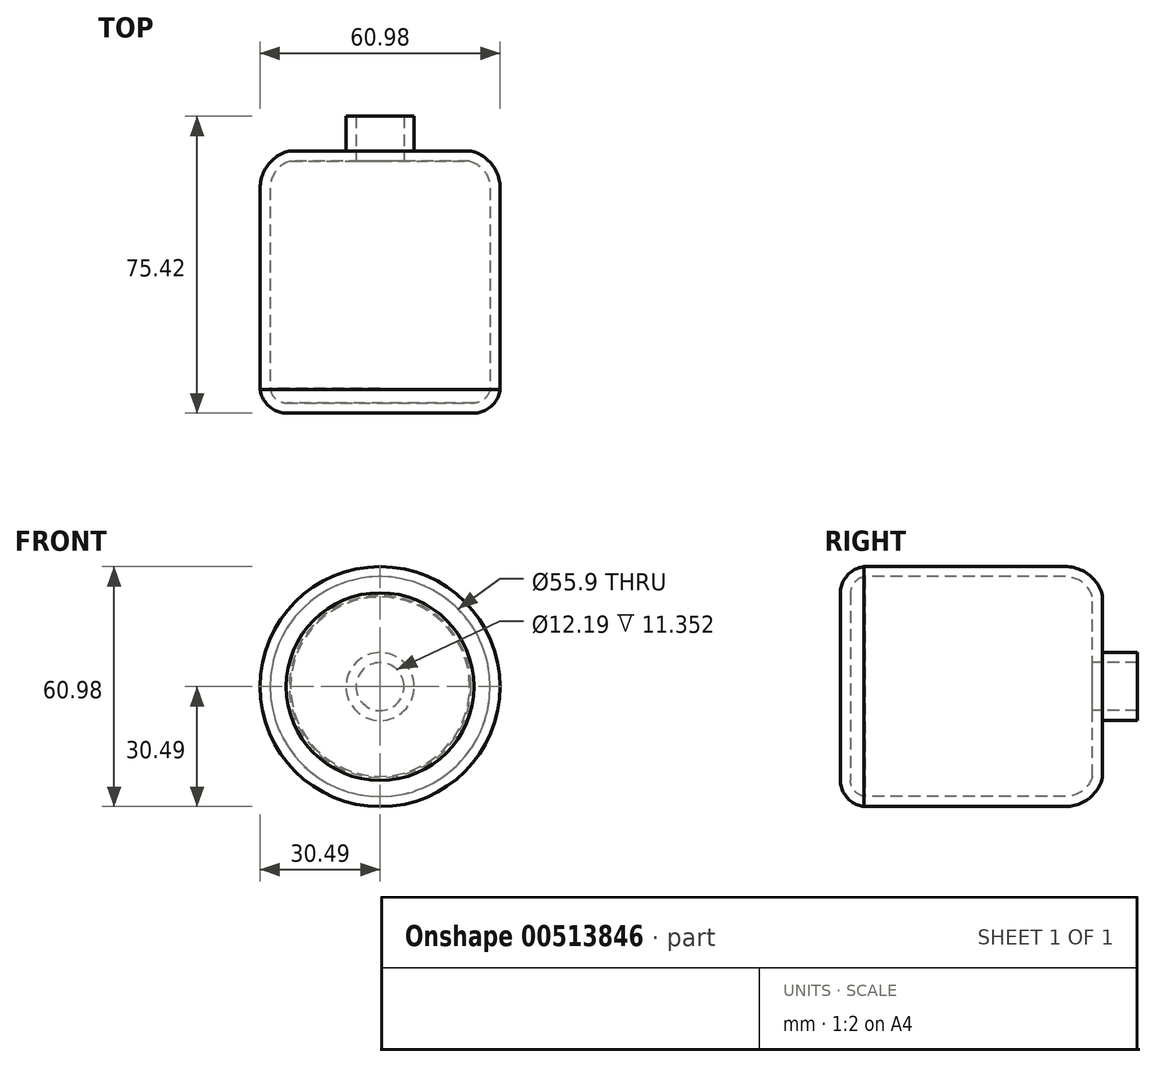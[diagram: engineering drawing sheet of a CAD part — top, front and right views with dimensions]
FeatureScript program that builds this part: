
annotation { "Feature Type Name" : "Feature", "Feature Type Description" : "" }
export const myFeature = defineFeature(function(context is Context, id is Id, definition is map)
    precondition{}
    {
        {
            var Q0;
            Q0=qCreatedBy(makeId("Top.planeOp"),FACE);
            var sketch = newSketch(context, id + "F0", { "sketchPlane" : qUnion([Q0])});
            skLineSegment(sketch, "E0", {"start": v(0, 64.85) * mm, "end": v(8.64, 64.85) * mm});
            skLineSegment(sketch, "E1", {"start": v(8.64, 64.85) * mm, "end": v(8.64, 58.86) * mm});
            skLineSegment(sketch, "E2", {"start": v(8.64, 58.86) * mm, "end": v(8.64, 56.04) * mm});
            skLineSegment(sketch, "E3", {"start": v(8.64, 56.04) * mm, "end": v(23.09, 56.04) * mm});
            skLineSegment(sketch, "E4", {"start": v(30.49, 46.56) * mm, "end": v(30.49, -4.53) * mm});
            skLineSegment(sketch, "E5", {"start": v(23.84, -10.57) * mm, "end": v(0, -10.57) * mm});
            skLineSegment(sketch, "E6", {"start": v(0, -10.57) * mm, "end": v(0, 64.85) * mm});
            skArc(sketch, "E7", {"start": v(23.44, -10.57) * mm, "mid": v(28.75, -8.32) * mm, "end": v(30.49, -2.82) * mm});
            skArc(sketch, "E8", {"start": v(30.49, 46.56) * mm, "mid": v(28.42, 52.58) * mm, "end": v(23.09, 56.04) * mm});
            skSolve(sketch);
        }
        {
            var Q0;
            Q0=makeQuery(id+"F0.imprint","IMPRINT",FACE,{"disambiguationData":[TD([[makeQuery(id+"F0.imprint","IMPRINT",EDGE,{"derivedFrom":sQuery(id+"F0.wireOp",EDGE,"E0")}),-1.0]])]});
            var Q1;
            Q1=sQuery(id+"F0.wireOp",EDGE,"E6");
            revolve(context, id + "F1", {"entities" : qUnion([Q0]), "axis" : qUnion([Q1]), "revolveType" : RevolveType.FULL});
        }
        {
            var Q0;
            Q0=makeQuery(id+"F1.opRevolve","SWEPT_FACE",FACE,{"disambiguationData":[OSD([sQuery(id+"F0.wireOp",EDGE,"E0")])]});
            shell(context, id + "F2", {"entities" : qUnion([Q0]), "thickness" : 2.54 * mm});
        }
    });
